# Revit family: CADS_AIRFLOWdev_AirflexPro_Round_StraightCeilingOutlet_Supply
name_source: partatom
category: Duct Fittings
units: mm (PartAtom-declared; Revit-internal decimal feet)

## family parameters
Always vertical = Yes
Cut with Voids When Loaded = No
Part Type = Wye
Round Connector Dimension = Use Diameter
Shared = No
Work Plane-Based = No

## types (2) — shared parameters
AF_Body = AF_Grey
CEApproval = Yes
ISO140001 = Yes
ISO90001 = Yes
Manufacturer = Airflow Developments Ltd
RunID = 0
SAPApproval = Yes
zero-valued in all types: CADS_Index

## per-type parameters (varying)
- CADS_AIRFLOWdev_AirFlex_Round_WallPlenum: AirflowRateRange=0.0 L/s; ExpectedServiceLife=0; FireControlPanelLinks=Yes; GrossWeight=0.00 kg; IsExtendedWarranty=Yes; NominalHeight=0 mm  [stored 0 ft]; NominalLength=0 mm  [stored 0 ft]; NominalWidth=0 mm  [stored 0 ft]; PassiveHouseApproval=Yes; Quantity=0; RedDotDesignAward=Yes; ShippingWeight=0.00 kg; WorkingPressure=0.0 Pa
- CADS_AIRFLOWdev_AirflexPro_Round_StraightCeilingOutlet_Supply: 6MonthlyMaintenance=Visually inspect system, clean the fan and ducting if necessary; AirflowRateRange=18.0 L/s; AssemblyPlace=UNKNOWN; AssetType=FIXED; Color=Silver; Constituents=Round straight ceiling/wall plenum; DurationUnit=Year; ExpectedServiceLife=10; Features=Round straight ceiling/wall plenum; Finish=Lacquer; FireControlPanelLinks=No; Fitting Type=Ignore; Grade=Stainless; GrossWeight=1.20 kg; IsExtendedWarranty=No; LongitudinalSeam=None; ManufacturerAddress=Aidelle House
Lancaster Road
Cressex Business Park
High Wycombe
Bucks
HP123QP; ManufacturerTelephone=01494 525252; ManufacturerWebsite=www.airflow.com; Material=Steel; NBSCode=45-80-50/394 Ventilation ducts; NominalHeight=150 mm; NominalLength=445 mm; NominalWidth=200 mm; PassiveHouseApproval=No; PointOfContact=Airflow Developments Ltd; ProductLiterature=https://www.airflow.com; ProductionYear=2017; Quantity=1; RedDotDesignAward=No; ReplacementCost=79.104; ServiceLifeDuration=10; ServiceLifeType=EXPECTEDSERVICELIFE; Shape=Other; ShippingWeight=1.44 kg; Size=445 x 200 x 150; Status=New; TemperatureRange=up to 40°C; Uniclass2015=Pr_30_59_96_92:Ventilation ducts; WarrantyGuarantor=Airflow Developments Ltd; WarrantyPeriod=0; WorkingPressure=3000.0 Pa

note: [stored X ft] marks values corroborated as IEEE doubles in the binary element streams (Revit-internal decimal feet)

## geometry (parser evidence)
native form markers: Blend x4, Sweep x2
no freeform markers — native parametric forms only
